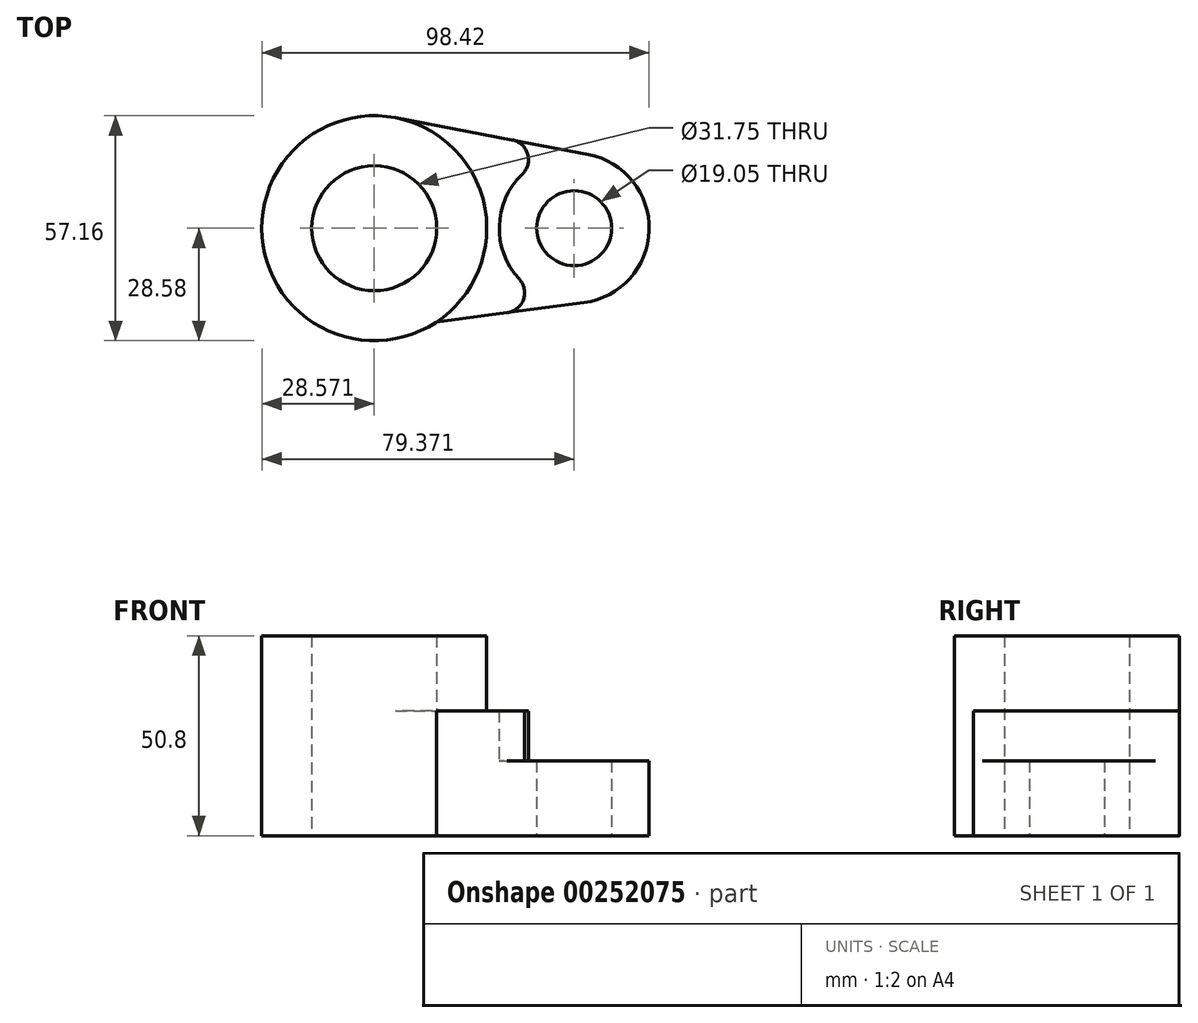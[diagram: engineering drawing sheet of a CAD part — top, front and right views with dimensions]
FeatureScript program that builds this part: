
annotation { "Feature Type Name" : "Feature", "Feature Type Description" : "" }
export const myFeature = defineFeature(function(context is Context, id is Id, definition is map)
    precondition{}
    {
        {
            var Q0;
            Q0=qCreatedBy(makeId("Top.planeOp"),FACE);
            var sketch = newSketch(context, id + "F0", { "sketchPlane" : qUnion([Q0])});
            skCircle(sketch, "E0", {"center": v(-41.76, 0) * mm, "radius": 15.87 * mm});
            skCircle(sketch, "E1", {"center": v(-41.76, 0) * mm, "radius": 28.58 * mm});
            skCircle(sketch, "E2", {"center": v(9.04, 0) * mm, "radius": 9.53 * mm});
            skCircle(sketch, "E3", {"center": v(9.04, 0) * mm, "radius": 19.05 * mm});
            skLineSegment(sketch, "E4", {"start": v(-36.4, 28.07) * mm, "end": v(12.61, 18.71) * mm});
            skLineSegment(sketch, "E5", {"start": v(-25.97, -23.82) * mm, "end": v(11.53, -18.89) * mm});
            skSolve(sketch);
        }
        {
            var Q0;
            Q0=makeQuery(id+"F0.imprint","IMPRINT",FACE,{"disambiguationData":[TD([[makeQuery(id+"F0.imprint","IMPRINT",EDGE,{"derivedFrom":sQuery(id+"F0.wireOp",EDGE,"E0")}),-1.0]])]});
            extrude(context, id + "F1", {"entities" : qUnion([Q0]), "depth" : 50.8 * mm});
        }
        {
            var Q0;
            {var subQ0=sQuery(id+"F0.wireOp",EDGE,"E4");Q0=makeQuery(id+"F0.imprint","IMPRINT",FACE,{"disambiguationData":[TD([[makeQuery(id+"F0.imprint","IMPRINT",EDGE,{"derivedFrom":subQ0}),-1.0]])]});}
            extrude(context, id + "F2", {"entities" : qUnion([Q0]), "operationType" : NewBodyOperationType.ADD, "depth" : 31.75 * mm});
        }
        {
            var Q0;
            Q0=makeQuery(id+"F0.imprint","IMPRINT",FACE,{"disambiguationData":[TD([[makeQuery(id+"F0.imprint","IMPRINT",EDGE,{"derivedFrom":sQuery(id+"F0.wireOp",EDGE,"E2")}),-1.0]])]});
            extrude(context, id + "F3", {"entities" : qUnion([Q0]), "operationType" : NewBodyOperationType.ADD, "depth" : 19.05 * mm});
        }
        {
            var Q0;
            {var subQ0=sQuery(id+"F0.wireOp",EDGE,"E3");var subQ1=sQuery(id+"F0.wireOp",EDGE,"E4");Q0=makeQuery(id+"F3.boolean.opBoolean","SPLIT",EDGE,{"disambiguationData":[TD([makeQuery(id+"F2.opExtrude","CAP_FACE",FACE,{"disambiguationData":[OSD([sQuery(id+"F0.wireOp",EDGE,"E1"),subQ0,subQ1,sQuery(id+"F0.wireOp",EDGE,"E5")])],"isStart":false})])],"derivedFrom":makeQuery(id+"F2.opExtrude","SWEPT_EDGE",EDGE,{"disambiguationData":[OSD([subQ0,subQ1])]})});}
            var Q1;
            {var subQ0=sQuery(id+"F0.wireOp",EDGE,"E3");var subQ1=sQuery(id+"F0.wireOp",EDGE,"E5");Q1=makeQuery(id+"F3.boolean.opBoolean","SPLIT",EDGE,{"disambiguationData":[TD([makeQuery(id+"F2.opExtrude","CAP_FACE",FACE,{"disambiguationData":[OSD([sQuery(id+"F0.wireOp",EDGE,"E1"),subQ0,sQuery(id+"F0.wireOp",EDGE,"E4"),subQ1])],"isStart":false})])],"derivedFrom":makeQuery(id+"F2.opExtrude","SWEPT_EDGE",EDGE,{"disambiguationData":[OSD([subQ0,subQ1])]})});}
            fillet(context, id + "F4", {"entities" : qUnion([Q0, Q1]), "radius" : 5.08 * mm, "tangentPropagation" : true, "allowEdgeOverflow" : false});
        }
    });
